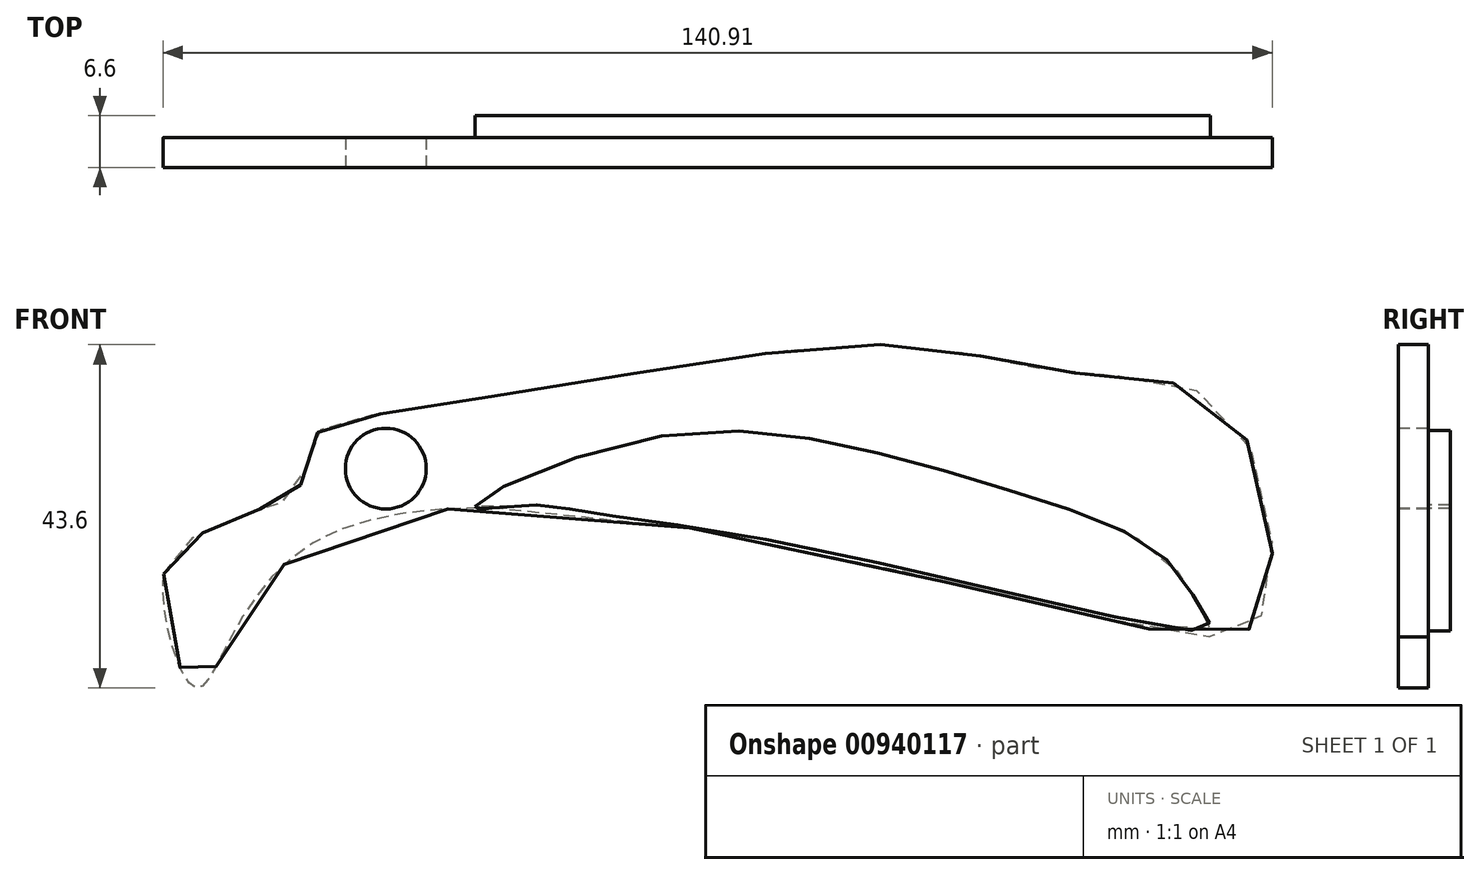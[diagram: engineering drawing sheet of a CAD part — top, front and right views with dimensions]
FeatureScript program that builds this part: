
annotation { "Feature Type Name" : "Feature", "Feature Type Description" : "" }
export const myFeature = defineFeature(function(context is Context, id is Id, definition is map)
    precondition{}
    {
        {
            var Q0;
            Q0=qCreatedBy(makeId("Front.planeOp"),FACE);
            var sketch = newSketch(context, id + "F0", { "sketchPlane" : qUnion([Q0])});
            skFitSpline(sketch, "E0", {"points": [v(-71.04, 0) * mm, v(-66.12, 5.2) * mm, v(-58.3, 8.4) * mm, v(-53.97, 10.7) * mm, v(-51.94, 17.36) * mm, v(-44.13, 20.26) * mm, v(-7.67, 26.04) * mm, v(24.16, 28.94) * mm, v(45, 25.46) * mm, v(64.1, 20.55) * mm, v(69.01, -3.76) * mm, v(57.15, -7.52) * mm, v(-51.36, 4.34) * mm, v(-66.99, -14.47) * mm, v(-71.04, 0) * mm]});
            skSolve(sketch);
        }
        {
            var Q0;
            Q0=makeQuery(id+"F0.imprint","IMPRINT",FACE,{"disambiguationData":[TD([[makeQuery(id+"F0.imprint","IMPRINT",EDGE,{"derivedFrom":sQuery(id+"F0.wireOp",EDGE,"E0")}),-1.0]])]});
            extrude(context, id + "F1", {"entities" : qUnion([Q0]), "depth" : 3.8 * mm, "offsetDistance" : 25.4 * mm});
        }
        {
            var Q0;
            Q0=makeQuery(id+"F1.opExtrude","CAP_FACE",FACE,{"disambiguationData":[OSD([sQuery(id+"F0.wireOp",EDGE,"E0")])],"isStart":false});
            var sketch = newSketch(context, id + "F2", { "sketchPlane" : qUnion([Q0])});
            skCircle(sketch, "E1", {"center": v(-42.84, 13.37) * mm, "radius": 5.13 * mm});
            skSolve(sketch);
        }
        {
            var Q0;
            Q0 = qSketchRegion(id + "F2", true);
            extrude(context, id + "F3", {"entities" : qUnion([Q0]), "operationType" : NewBodyOperationType.REMOVE, "oppositeDirection" : true, "depth" : 104.14 * mm, "offsetDistance" : 25.4 * mm});
        }
        {
            var Q0;
            Q0=qCreatedBy(makeId("Front.planeOp"),FACE);
            var sketch = newSketch(context, id + "F4", { "sketchPlane" : qUnion([Q0])});
            skFitSpline(sketch, "E2", {"points": [v(-31.5, 8.56) * mm, v(-10.94, 16.93) * mm, v(17.8, 15.8) * mm, v(41, 9.13) * mm, v(56.23, 1.9) * mm, v(61.17, -5.33) * mm, v(61.74, -7.04) * mm, v(11.32, 3.23) * mm, v(-18.17, 8) * mm, v(-24.45, 8.75) * mm, v(-31.5, 8.56) * mm]});
            skSolve(sketch);
        }
        {
            var Q0;
            Q0 = qSketchRegion(id + "F4", true);
            extrude(context, id + "F5", {"entities" : qUnion([Q0]), "operationType" : NewBodyOperationType.ADD, "oppositeDirection" : true, "depth" : 2.8 * mm, "offsetDistance" : 25.4 * mm});
        }
    });
